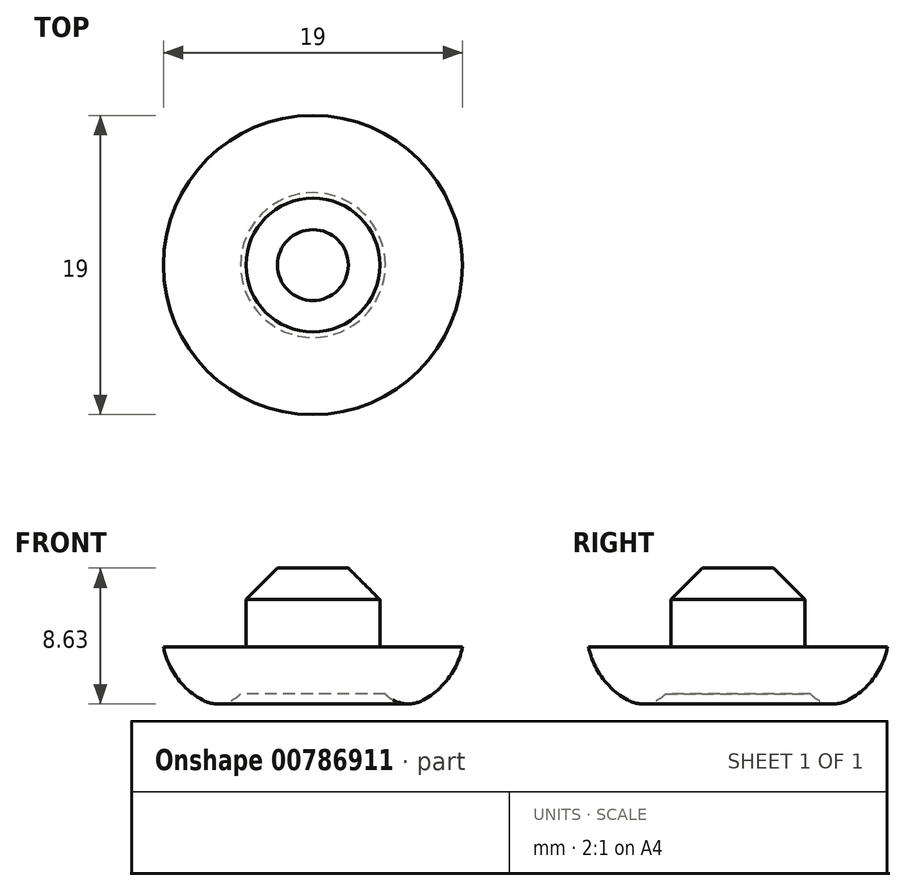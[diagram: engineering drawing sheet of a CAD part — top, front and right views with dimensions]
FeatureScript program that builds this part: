
annotation { "Feature Type Name" : "Feature", "Feature Type Description" : "" }
export const myFeature = defineFeature(function(context is Context, id is Id, definition is map)
    precondition{}
    {
        {
            var Q0;
            Q0=qCreatedBy(makeId("Top.planeOp"),FACE);
            var sketch = newSketch(context, id + "F0", { "sketchPlane" : qUnion([Q0])});
            skCircle(sketch, "E0", {"center": v(0, 0) * mm, "radius": 9.5 * mm});
            skSolve(sketch);
        }
        {
            var Q0;
            Q0=makeQuery(id+"F0.imprint","IMPRINT",FACE,{"disambiguationData":[TD([[makeQuery(id+"F0.imprint","IMPRINT",EDGE,{"derivedFrom":sQuery(id+"F0.wireOp",EDGE,"E0")}),1.0]])]});
            extrude(context, id + "F1", {"entities" : qUnion([Q0]), "depth" : 4 * mm, "offsetDistance" : 25 * mm});
        }
        {
            var Q0;
            Q0=makeQuery(id+"F1.opExtrude","CAP_FACE",FACE,{"disambiguationData":[OSD([sQuery(id+"F0.wireOp",EDGE,"E0")])],"isStart":false});
            var sketch = newSketch(context, id + "F2", { "sketchPlane" : qUnion([Q0])});
            skCircle(sketch, "E1", {"center": v(0, 0) * mm, "radius": 4.25 * mm});
            skSolve(sketch);
        }
        {
            var Q0;
            Q0=makeQuery(id+"F2.imprint","IMPRINT",FACE,{"disambiguationData":[TD([[makeQuery(id+"F2.imprint","IMPRINT",EDGE,{"derivedFrom":sQuery(id+"F2.wireOp",EDGE,"E1")}),1.0]])]});
            extrude(context, id + "F3", {"entities" : qUnion([Q0]), "operationType" : NewBodyOperationType.ADD, "depth" : 5 * mm, "offsetDistance" : 25 * mm});
        }
        {
            var Q0;
            Q0=makeQuery(id+"F1.opExtrude","CAP_EDGE",EDGE,{"disambiguationData":[OSD([sQuery(id+"F0.wireOp",EDGE,"E0")])],"isStart":true});
            fillet(context, id + "F4", {"entities" : qUnion([Q0]), "radius" : 5 * mm, "tangentPropagation" : true, "allowEdgeOverflow" : false});
        }
        {
            var Q0;
            Q0=makeQuery(id+"F3.opExtrude","CAP_EDGE",EDGE,{"disambiguationData":[OSD([sQuery(id+"F2.wireOp",EDGE,"E1")])],"isStart":false});
            chamfer(context, id + "F5", {"entities" : qUnion([Q0]), "width" : 2 * mm, "tangentPropagation" : true});
        }
        {
            var Q0;
            Q0=makeQuery(id+"F1.opExtrude","CAP_FACE",FACE,{"disambiguationData":[OSD([sQuery(id+"F0.wireOp",EDGE,"E0")])],"isStart":true});
            extrude(context, id + "F6", {"entities" : qUnion([Q0]), "operationType" : NewBodyOperationType.REMOVE, "oppositeDirection" : true, "depth" : 1 * mm, "offsetDistance" : 25 * mm});
        }
        {
            var Q0;
            {var subQ0=sQuery(id+"F0.wireOp",EDGE,"E0");Q0=makeQuery(id+"F6.boolean.opBoolean","MERGE",EDGE,{"derivedFrom":[makeQuery(id+"F4.opFillet","BLEND_EDGE",EDGE,{"blendedFrom":[makeQuery(id+"F1.opExtrude","CAP_EDGE",EDGE,{"disambiguationData":[OSD([subQ0])],"isStart":true}),makeQuery(id+"F1.opExtrude","CAP_FACE",FACE,{"disambiguationData":[OSD([subQ0])],"isStart":true})],"blendedInto":[makeQuery(id+"F1.opExtrude","CAP_FACE",FACE,{"disambiguationData":[OSD([subQ0])],"isStart":true})]}),makeQuery(id+"F6.opExtrude","CAP_EDGE",EDGE,{"disambiguationData":[OSD([subQ0])],"isStart":true})]});}
            fillet(context, id + "F7", {"entities" : qUnion([Q0]), "radius" : 2 * mm, "tangentPropagation" : true, "allowEdgeOverflow" : false});
        }
    });
